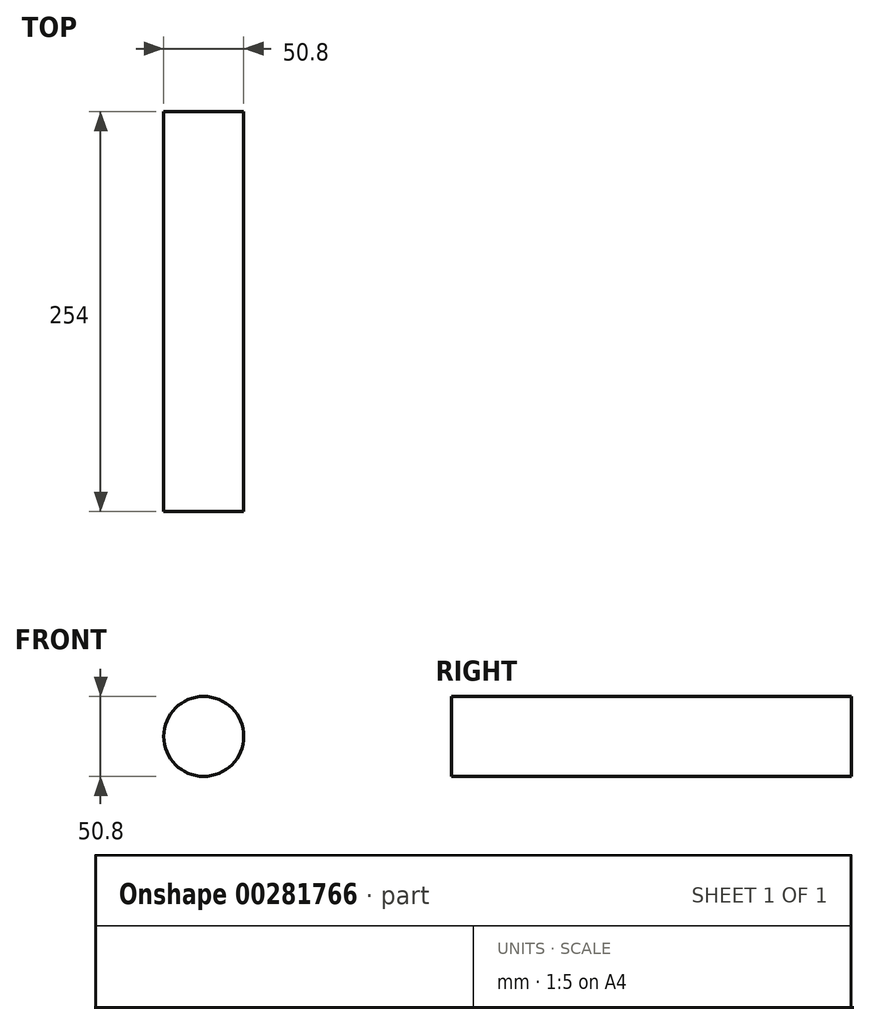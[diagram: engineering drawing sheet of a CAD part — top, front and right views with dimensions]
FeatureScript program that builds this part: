
annotation { "Feature Type Name" : "Feature", "Feature Type Description" : "" }
export const myFeature = defineFeature(function(context is Context, id is Id, definition is map)
    precondition{}
    {
        {
            var Q0;
            Q0=qCreatedBy(makeId("Front.planeOp"),FACE);
            var sketch = newSketch(context, id + "F0", { "sketchPlane" : qUnion([Q0])});
            skCircle(sketch, "E0", {"center": v(0, 0) * mm, "radius": 25.4 * mm});
            skSolve(sketch);
        }
        {
            var Q0;
            Q0 = qSketchRegion(id + "F0", true);
            extrude(context, id + "F1", {"entities" : qUnion([Q0]), "depth" : 254 * mm});
        }
    });
